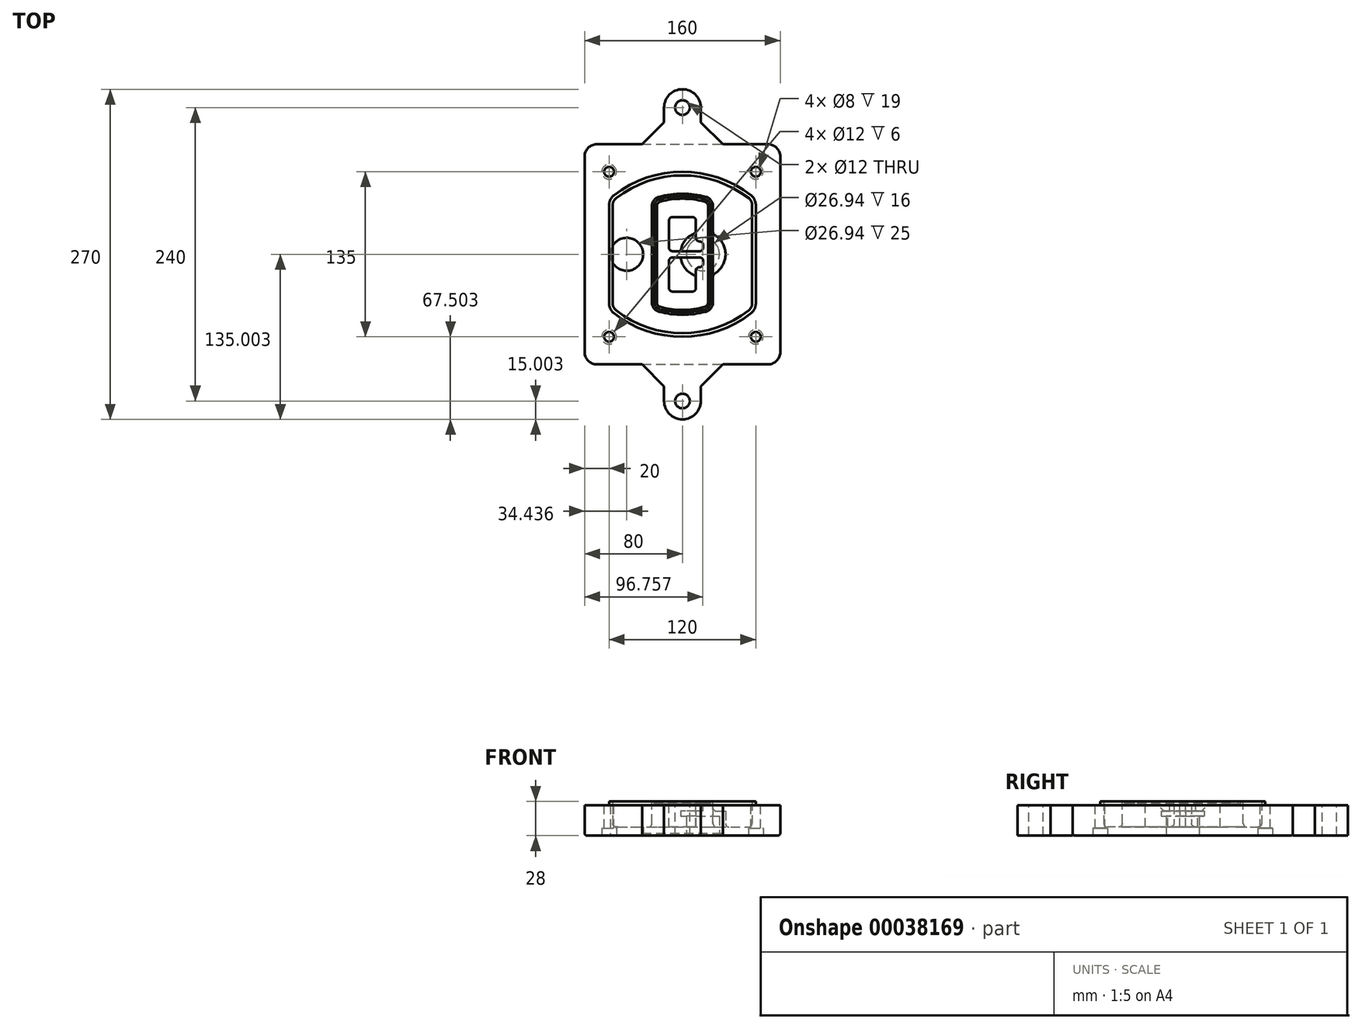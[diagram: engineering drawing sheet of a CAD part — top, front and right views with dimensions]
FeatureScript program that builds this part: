
annotation { "Feature Type Name" : "Feature", "Feature Type Description" : "" }
export const myFeature = defineFeature(function(context is Context, id is Id, definition is map)
    precondition{}
    {
        {
            var Q0;
            Q0=qCreatedBy(makeId("Top.planeOp"),FACE);
            var sketch = newSketch(context, id + "F0", { "sketchPlane" : qUnion([Q0])});
            skPoint(sketch, "E0.rect.middle", {"position": v(0, 0) * mm});
            skLineSegment(sketch, "E1.bottom", {"start": v(24.05, 28.38) * mm, "end": v(164.05, 28.38) * mm});
            skLineSegment(sketch, "E1.top", {"start": v(24.05, 208.38) * mm, "end": v(164.05, 208.38) * mm});
            skLineSegment(sketch, "E1.left", {"start": v(14.05, 38.38) * mm, "end": v(14.05, 198.38) * mm});
            skLineSegment(sketch, "E1.right", {"start": v(174.05, 38.38) * mm, "end": v(174.05, 198.38) * mm});
            skLineSegment(sketch, "E2", {"start": v(14.05, 208.38) * mm, "end": v(174.05, 28.38) * mm, "construction": true});
            skLineSegment(sketch, "E3", {"start": v(174.05, 208.38) * mm, "end": v(14.05, 28.38) * mm, "construction": true});
            skCircle(sketch, "E4", {"center": v(34.05, 185.88) * mm, "radius": 4 * mm});
            skCircle(sketch, "E5", {"center": v(154.05, 185.88) * mm, "radius": 4 * mm});
            skCircle(sketch, "E6", {"center": v(154.05, 50.88) * mm, "radius": 4 * mm});
            skCircle(sketch, "E7", {"center": v(34.05, 50.88) * mm, "radius": 4 * mm});
            skLineSegment(sketch, "E8", {"start": v(34.05, 185.88) * mm, "end": v(154.05, 185.88) * mm, "construction": true});
            skLineSegment(sketch, "E9", {"start": v(154.05, 185.88) * mm, "end": v(154.05, 50.88) * mm, "construction": true});
            skLineSegment(sketch, "E10", {"start": v(154.05, 50.88) * mm, "end": v(34.05, 50.88) * mm, "construction": true});
            skLineSegment(sketch, "E11", {"start": v(34.05, 50.88) * mm, "end": v(34.05, 185.88) * mm, "construction": true});
            skLineSegment(sketch, "E12", {"start": v(34.05, 158.68) * mm, "end": v(34.05, 78.09) * mm});
            skLineSegment(sketch, "E13", {"start": v(154.05, 158.68) * mm, "end": v(154.05, 78.09) * mm});
            skArc(sketch, "E14", {"start": v(150.2, 166.56) * mm, "mid": v(94.05, 185.88) * mm, "end": v(37.9, 166.56) * mm});
            skArc(sketch, "E15", {"start": v(37.9, 70.2) * mm, "mid": v(94.05, 50.88) * mm, "end": v(150.2, 70.2) * mm});
            skLineSegment(sketch, "E16", {"start": v(34.05, 118.38) * mm, "end": v(154.05, 118.38) * mm, "construction": true});
            skPoint(sketch, "E17.visualSharp", {"position": v(34.05, 73.38) * mm});
            skArc(sketch, "E17.filletArc", {"start": v(34.05, 78.09) * mm, "mid": v(35.06, 73.7) * mm, "end": v(37.9, 70.2) * mm});
            skPoint(sketch, "E18.visualSharp", {"position": v(34.05, 163.38) * mm});
            skArc(sketch, "E18.filletArc", {"start": v(37.9, 166.56) * mm, "mid": v(35.06, 163.06) * mm, "end": v(34.05, 158.68) * mm});
            skPoint(sketch, "E19.visualSharp", {"position": v(154.05, 163.38) * mm});
            skArc(sketch, "E19.filletArc", {"start": v(154.05, 158.68) * mm, "mid": v(153.04, 163.06) * mm, "end": v(150.2, 166.56) * mm});
            skPoint(sketch, "E20.visualSharp", {"position": v(154.05, 73.38) * mm});
            skArc(sketch, "E20.filletArc", {"start": v(150.2, 70.2) * mm, "mid": v(153.04, 73.7) * mm, "end": v(154.05, 78.09) * mm});
            skPoint(sketch, "E21.visualSharp", {"position": v(14.05, 208.38) * mm});
            skArc(sketch, "E21.filletArc", {"start": v(24.05, 208.38) * mm, "mid": v(16.98, 205.45) * mm, "end": v(14.05, 198.38) * mm});
            skPoint(sketch, "E22.visualSharp", {"position": v(174.05, 208.38) * mm});
            skArc(sketch, "E22.filletArc", {"start": v(174.05, 198.38) * mm, "mid": v(171.12, 205.45) * mm, "end": v(164.05, 208.38) * mm});
            skPoint(sketch, "E23.visualSharp", {"position": v(174.05, 28.38) * mm});
            skArc(sketch, "E23.filletArc", {"start": v(164.05, 28.38) * mm, "mid": v(171.12, 31.31) * mm, "end": v(174.05, 38.38) * mm});
            skPoint(sketch, "E24.visualSharp", {"position": v(14.05, 28.38) * mm});
            skArc(sketch, "E24.filletArc", {"start": v(14.05, 38.38) * mm, "mid": v(16.98, 31.31) * mm, "end": v(24.05, 28.38) * mm});
            skArc(sketch, "E25.0", {"start": v(151.05, 158.68) * mm, "mid": v(150.34, 161.75) * mm, "end": v(148.36, 164.2) * mm});
            skLineSegment(sketch, "E25.1", {"start": v(151.05, 158.68) * mm, "end": v(151.05, 78.09) * mm});
            skArc(sketch, "E25.2", {"start": v(148.36, 72.57) * mm, "mid": v(150.34, 75.02) * mm, "end": v(151.05, 78.09) * mm});
            skArc(sketch, "E25.3", {"start": v(39.74, 72.57) * mm, "mid": v(94.05, 53.88) * mm, "end": v(148.36, 72.57) * mm});
            skArc(sketch, "E25.4", {"start": v(37.05, 78.09) * mm, "mid": v(37.76, 75.02) * mm, "end": v(39.74, 72.57) * mm});
            skArc(sketch, "E25.5", {"start": v(148.36, 164.2) * mm, "mid": v(94.05, 182.88) * mm, "end": v(39.74, 164.2) * mm});
            skLineSegment(sketch, "E25.6", {"start": v(37.05, 158.68) * mm, "end": v(37.05, 78.09) * mm});
            skArc(sketch, "E25.7", {"start": v(39.74, 164.2) * mm, "mid": v(37.76, 161.75) * mm, "end": v(37.05, 158.68) * mm});
            skArc(sketch, "E26.0", {"start": v(35.43, 169.71) * mm, "mid": v(31.47, 164.82) * mm, "end": v(30.05, 158.68) * mm});
            skArc(sketch, "E26.1", {"start": v(152.67, 169.71) * mm, "mid": v(94.05, 189.88) * mm, "end": v(35.43, 169.71) * mm});
            skArc(sketch, "E26.2", {"start": v(158.05, 158.68) * mm, "mid": v(156.63, 164.82) * mm, "end": v(152.67, 169.71) * mm});
            skLineSegment(sketch, "E26.3", {"start": v(158.05, 158.68) * mm, "end": v(158.05, 78.09) * mm});
            skArc(sketch, "E26.4", {"start": v(152.67, 67.05) * mm, "mid": v(156.63, 71.95) * mm, "end": v(158.05, 78.09) * mm});
            skLineSegment(sketch, "E26.5", {"start": v(30.05, 158.68) * mm, "end": v(30.05, 78.09) * mm});
            skArc(sketch, "E26.6", {"start": v(35.43, 67.05) * mm, "mid": v(94.05, 46.88) * mm, "end": v(152.67, 67.05) * mm});
            skArc(sketch, "E26.7", {"start": v(30.05, 78.09) * mm, "mid": v(31.47, 71.95) * mm, "end": v(35.43, 67.05) * mm});
            skSolve(sketch);
        }
        {
            var Q0;
            Q0=makeQuery(id+"F0.imprint","IMPRINT",FACE,{"disambiguationData":[TD([[makeQuery(id+"F0.imprint","IMPRINT",EDGE,{"derivedFrom":sQuery(id+"F0.wireOp",EDGE,"E1.bottom")}),1.0]])]});
            var Q1;
            Q1=makeQuery(id+"F0.imprint","IMPRINT",FACE,{"disambiguationData":[TD([[makeQuery(id+"F0.imprint","IMPRINT",EDGE,{"derivedFrom":sQuery(id+"F0.wireOp",EDGE,"E12")}),1.0]])]});
            var Q2;
            Q2=makeQuery(id+"F0.imprint","IMPRINT",FACE,{"disambiguationData":[TD([[makeQuery(id+"F0.imprint","IMPRINT",EDGE,{"derivedFrom":sQuery(id+"F0.wireOp",EDGE,"E25.0")}),1.0]])]});
            var Q3;
            Q3=makeQuery(id+"F0.imprint","IMPRINT",FACE,{"disambiguationData":[TD([[makeQuery(id+"F0.imprint","IMPRINT",EDGE,{"derivedFrom":sQuery(id+"F0.wireOp",EDGE,"E12")}),-1.0]])]});
            extrude(context, id + "F1", {"entities" : qUnion([Q0, Q1, Q2, Q3]), "oppositeDirection" : true, "depth" : 25 * mm});
        }
        {
            var Q0;
            Q0=makeQuery(id+"F0.imprint","IMPRINT",FACE,{"disambiguationData":[TD([[makeQuery(id+"F0.imprint","IMPRINT",EDGE,{"derivedFrom":sQuery(id+"F0.wireOp",EDGE,"E12")}),1.0]])]});
            extrude(context, id + "F2", {"entities" : qUnion([Q0]), "operationType" : NewBodyOperationType.ADD, "depth" : 3 * mm});
        }
        {
            var Q0;
            Q0=makeQuery(id+"F0.imprint","IMPRINT",FACE,{"disambiguationData":[TD([[makeQuery(id+"F0.imprint","IMPRINT",EDGE,{"derivedFrom":sQuery(id+"F0.wireOp",EDGE,"E25.0")}),1.0]])]});
            extrude(context, id + "F3", {"entities" : qUnion([Q0]), "operationType" : NewBodyOperationType.REMOVE, "oppositeDirection" : true, "depth" : 18 * mm});
        }
        {
            var Q0;
            Q0=makeQuery(id+"F2.opExtrude","CAP_FACE",FACE,{"disambiguationData":[OSD([sQuery(id+"F0.wireOp",EDGE,"E12"),sQuery(id+"F0.wireOp",EDGE,"E13"),sQuery(id+"F0.wireOp",EDGE,"E14"),sQuery(id+"F0.wireOp",EDGE,"E15"),sQuery(id+"F0.wireOp",EDGE,"E17.filletArc"),sQuery(id+"F0.wireOp",EDGE,"E18.filletArc"),sQuery(id+"F0.wireOp",EDGE,"E19.filletArc"),sQuery(id+"F0.wireOp",EDGE,"E20.filletArc"),sQuery(id+"F0.wireOp",EDGE,"E25.0"),sQuery(id+"F0.wireOp",EDGE,"E25.1"),sQuery(id+"F0.wireOp",EDGE,"E25.2"),sQuery(id+"F0.wireOp",EDGE,"E25.3"),sQuery(id+"F0.wireOp",EDGE,"E25.4"),sQuery(id+"F0.wireOp",EDGE,"E25.5"),sQuery(id+"F0.wireOp",EDGE,"E25.6"),sQuery(id+"F0.wireOp",EDGE,"E25.7")])],"isStart":false});
            var sketch = newSketch(context, id + "F4", { "sketchPlane" : qUnion([Q0])});
            skArc(sketch, "E27.0", {"start": v(74.97, 71.41) * mm, "mid": v(94.05, 68.88) * mm, "end": v(113.13, 71.41) * mm});
            skArc(sketch, "E28.0", {"start": v(113.13, 165.35) * mm, "mid": v(94.05, 167.88) * mm, "end": v(74.97, 165.35) * mm});
            skLineSegment(sketch, "E29", {"start": v(69.05, 157.63) * mm, "end": v(69.05, 79.14) * mm});
            skLineSegment(sketch, "E30", {"start": v(119.05, 157.63) * mm, "end": v(119.05, 79.14) * mm});
            skLineSegment(sketch, "E31", {"start": v(69.05, 163.48) * mm, "end": v(119.05, 163.48) * mm, "construction": true});
            skLineSegment(sketch, "E32", {"start": v(69.05, 73.28) * mm, "end": v(119.05, 73.28) * mm, "construction": true});
            skPoint(sketch, "E33.visualSharp", {"position": v(69.05, 163.48) * mm});
            skArc(sketch, "E33.filletArc", {"start": v(74.97, 165.35) * mm, "mid": v(70.7, 162.5) * mm, "end": v(69.05, 157.63) * mm});
            skPoint(sketch, "E34.visualSharp", {"position": v(119.05, 163.48) * mm});
            skArc(sketch, "E34.filletArc", {"start": v(119.05, 157.63) * mm, "mid": v(117.4, 162.5) * mm, "end": v(113.13, 165.35) * mm});
            skPoint(sketch, "E35.visualSharp", {"position": v(119.05, 73.28) * mm});
            skArc(sketch, "E35.filletArc", {"start": v(113.13, 71.41) * mm, "mid": v(117.4, 74.27) * mm, "end": v(119.05, 79.14) * mm});
            skPoint(sketch, "E36.visualSharp", {"position": v(69.05, 73.28) * mm});
            skArc(sketch, "E36.filletArc", {"start": v(69.05, 79.14) * mm, "mid": v(70.7, 74.27) * mm, "end": v(74.97, 71.41) * mm});
            skArc(sketch, "E37.0", {"start": v(148.36, 164.2) * mm, "mid": v(94.05, 182.88) * mm, "end": v(39.74, 164.2) * mm});
            skArc(sketch, "E37.1", {"start": v(39.74, 164.2) * mm, "mid": v(37.76, 161.75) * mm, "end": v(37.05, 158.68) * mm});
            skLineSegment(sketch, "E37.2", {"start": v(37.05, 158.68) * mm, "end": v(37.05, 78.09) * mm});
            skArc(sketch, "E37.3", {"start": v(37.05, 78.09) * mm, "mid": v(37.76, 75.02) * mm, "end": v(39.74, 72.57) * mm});
            skArc(sketch, "E37.4", {"start": v(39.74, 72.57) * mm, "mid": v(94.05, 53.88) * mm, "end": v(148.36, 72.57) * mm});
            skArc(sketch, "E37.5", {"start": v(148.36, 72.57) * mm, "mid": v(150.34, 75.02) * mm, "end": v(151.05, 78.09) * mm});
            skLineSegment(sketch, "E37.6", {"start": v(151.05, 158.68) * mm, "end": v(151.05, 78.09) * mm});
            skArc(sketch, "E37.7", {"start": v(151.05, 158.68) * mm, "mid": v(150.34, 161.75) * mm, "end": v(148.36, 164.2) * mm});
            skLineSegment(sketch, "E38.0", {"start": v(117.05, 157.63) * mm, "end": v(117.05, 79.14) * mm});
            skArc(sketch, "E38.1", {"start": v(112.61, 73.34) * mm, "mid": v(115.81, 75.49) * mm, "end": v(117.05, 79.14) * mm});
            skArc(sketch, "E38.2", {"start": v(75.49, 73.34) * mm, "mid": v(94.05, 70.88) * mm, "end": v(112.61, 73.34) * mm});
            skArc(sketch, "E38.3", {"start": v(71.05, 79.14) * mm, "mid": v(72.29, 75.49) * mm, "end": v(75.49, 73.34) * mm});
            skLineSegment(sketch, "E38.4", {"start": v(71.05, 157.63) * mm, "end": v(71.05, 79.14) * mm});
            skArc(sketch, "E38.5", {"start": v(117.05, 157.63) * mm, "mid": v(115.81, 161.28) * mm, "end": v(112.61, 163.42) * mm});
            skArc(sketch, "E38.6", {"start": v(75.49, 163.42) * mm, "mid": v(72.29, 161.28) * mm, "end": v(71.05, 157.63) * mm});
            skArc(sketch, "E38.7", {"start": v(112.61, 163.42) * mm, "mid": v(94.05, 165.88) * mm, "end": v(75.49, 163.42) * mm});
            skArc(sketch, "E39.0", {"start": v(115.05, 157.63) * mm, "mid": v(114.23, 160.06) * mm, "end": v(112.1, 161.5) * mm});
            skLineSegment(sketch, "E39.1", {"start": v(115.05, 157.63) * mm, "end": v(115.05, 79.14) * mm});
            skArc(sketch, "E39.2", {"start": v(112.1, 75.27) * mm, "mid": v(114.23, 76.7) * mm, "end": v(115.05, 79.14) * mm});
            skArc(sketch, "E39.3", {"start": v(76, 75.27) * mm, "mid": v(94.05, 72.88) * mm, "end": v(112.1, 75.27) * mm});
            skArc(sketch, "E39.4", {"start": v(73.05, 79.14) * mm, "mid": v(73.87, 76.7) * mm, "end": v(76, 75.27) * mm});
            skArc(sketch, "E39.5", {"start": v(112.1, 161.5) * mm, "mid": v(94.05, 163.88) * mm, "end": v(76, 161.5) * mm});
            skLineSegment(sketch, "E39.6", {"start": v(73.05, 157.63) * mm, "end": v(73.05, 79.14) * mm});
            skArc(sketch, "E39.7", {"start": v(76, 161.5) * mm, "mid": v(73.87, 160.06) * mm, "end": v(73.05, 157.63) * mm});
            skLineSegment(sketch, "E40", {"start": v(69.05, 118.38) * mm, "end": v(119.05, 118.38) * mm, "construction": true});
            skLineSegment(sketch, "E41", {"start": v(83.05, 123.88) * mm, "end": v(83.05, 145.88) * mm});
            skLineSegment(sketch, "E42", {"start": v(86.05, 148.88) * mm, "end": v(102.05, 148.88) * mm});
            skLineSegment(sketch, "E43", {"start": v(105.05, 145.88) * mm, "end": v(105.05, 131.88) * mm});
            skLineSegment(sketch, "E44", {"start": v(108.05, 128.88) * mm, "end": v(108.05, 128.88) * mm});
            skLineSegment(sketch, "E45", {"start": v(111.05, 125.88) * mm, "end": v(111.05, 123.88) * mm});
            skLineSegment(sketch, "E46", {"start": v(108.05, 120.88) * mm, "end": v(86.05, 120.88) * mm});
            skPoint(sketch, "E47.visualSharp", {"position": v(83.05, 148.88) * mm});
            skArc(sketch, "E47.filletArc", {"start": v(86.05, 148.88) * mm, "mid": v(83.93, 148) * mm, "end": v(83.05, 145.88) * mm});
            skPoint(sketch, "E48.visualSharp", {"position": v(105.05, 148.88) * mm});
            skArc(sketch, "E48.filletArc", {"start": v(105.05, 145.88) * mm, "mid": v(104.17, 148) * mm, "end": v(102.05, 148.88) * mm});
            skPoint(sketch, "E49.visualSharp", {"position": v(105.05, 128.88) * mm});
            skArc(sketch, "E49.filletArc", {"start": v(105.05, 131.88) * mm, "mid": v(105.93, 129.76) * mm, "end": v(108.05, 128.88) * mm});
            skPoint(sketch, "E50.visualSharp", {"position": v(111.05, 128.88) * mm});
            skArc(sketch, "E50.filletArc", {"start": v(111.05, 125.88) * mm, "mid": v(110.17, 128) * mm, "end": v(108.05, 128.88) * mm});
            skPoint(sketch, "E51.visualSharp", {"position": v(111.05, 120.88) * mm});
            skArc(sketch, "E51.filletArc", {"start": v(108.05, 120.88) * mm, "mid": v(110.17, 121.76) * mm, "end": v(111.05, 123.88) * mm});
            skPoint(sketch, "E52.visualSharp", {"position": v(83.05, 120.88) * mm});
            skArc(sketch, "E52.filletArc", {"start": v(83.05, 123.88) * mm, "mid": v(83.93, 121.76) * mm, "end": v(86.05, 120.88) * mm});
            skLineSegment(sketch, "E53.0.MirrorCS", {"start": v(108.05, 115.88) * mm, "end": v(86.05, 115.88) * mm});
            skArc(sketch, "E54.0.MirrorCS", {"start": v(83.05, 112.88) * mm, "mid": v(83.93, 115) * mm, "end": v(86.05, 115.88) * mm});
            skLineSegment(sketch, "E55.0.MirrorCS", {"start": v(83.05, 112.88) * mm, "end": v(83.05, 90.88) * mm});
            skArc(sketch, "E56.0.MirrorCS", {"start": v(86.05, 87.88) * mm, "mid": v(83.93, 88.76) * mm, "end": v(83.05, 90.88) * mm});
            skLineSegment(sketch, "E57.0.MirrorCS", {"start": v(86.05, 87.88) * mm, "end": v(102.05, 87.88) * mm});
            skArc(sketch, "E58.0.MirrorCS", {"start": v(105.05, 90.88) * mm, "mid": v(104.17, 88.76) * mm, "end": v(102.05, 87.88) * mm});
            skLineSegment(sketch, "E59.0.MirrorCS", {"start": v(105.05, 90.88) * mm, "end": v(105.05, 104.88) * mm});
            skArc(sketch, "E60.0.MirrorCS", {"start": v(105.05, 104.88) * mm, "mid": v(105.93, 107) * mm, "end": v(108.05, 107.88) * mm});
            skArc(sketch, "E61.0.MirrorCS", {"start": v(111.05, 110.88) * mm, "mid": v(110.17, 108.76) * mm, "end": v(108.05, 107.88) * mm});
            skLineSegment(sketch, "E62.0.MirrorCS", {"start": v(111.05, 110.88) * mm, "end": v(111.05, 112.88) * mm});
            skArc(sketch, "E63.0.MirrorCS", {"start": v(108.05, 115.88) * mm, "mid": v(110.17, 115) * mm, "end": v(111.05, 112.88) * mm});
            skSolve(sketch);
        }
        {
            var Q0;
            Q0=makeQuery(id+"F4.imprint","IMPRINT",FACE,{"disambiguationData":[TD([[makeQuery(id+"F4.imprint","IMPRINT",EDGE,{"derivedFrom":sQuery(id+"F4.wireOp",EDGE,"E27.0")}),1.0]])]});
            var Q1;
            Q1=makeQuery(id+"F4.imprint","IMPRINT",FACE,{"disambiguationData":[TD([[makeQuery(id+"F4.imprint","IMPRINT",EDGE,{"derivedFrom":sQuery(id+"F4.wireOp",EDGE,"E38.0")}),-1.0]])]});
            var Q2;
            Q2=makeQuery(id+"F4.imprint","IMPRINT",FACE,{"disambiguationData":[TD([[makeQuery(id+"F4.imprint","IMPRINT",EDGE,{"derivedFrom":sQuery(id+"F4.wireOp",EDGE,"E39.0")}),1.0]])]});
            extrude(context, id + "F5", {"entities" : qUnion([Q0, Q1, Q2]), "operationType" : NewBodyOperationType.ADD, "endBound" : BoundingType.UP_TO_NEXT, "oppositeDirection" : true, "depth" : 25 * mm});
        }
        {
            var Q0;
            Q0=makeQuery(id+"F4.imprint","IMPRINT",FACE,{"disambiguationData":[TD([[makeQuery(id+"F4.imprint","IMPRINT",EDGE,{"derivedFrom":sQuery(id+"F4.wireOp",EDGE,"E38.0")}),-1.0]])]});
            extrude(context, id + "F6", {"entities" : qUnion([Q0]), "operationType" : NewBodyOperationType.REMOVE, "oppositeDirection" : true, "depth" : 2 * mm});
        }
        {
            var Q0;
            Q0=makeQuery(id+"F1.opExtrude","CAP_FACE",FACE,{"disambiguationData":[OSD([sQuery(id+"F0.wireOp",EDGE,"E1.bottom"),sQuery(id+"F0.wireOp",EDGE,"E1.top"),sQuery(id+"F0.wireOp",EDGE,"E1.left"),sQuery(id+"F0.wireOp",EDGE,"E1.right"),sQuery(id+"F0.wireOp",EDGE,"E4"),sQuery(id+"F0.wireOp",EDGE,"E5"),sQuery(id+"F0.wireOp",EDGE,"E6"),sQuery(id+"F0.wireOp",EDGE,"E7"),sQuery(id+"F0.wireOp",EDGE,"E21.filletArc"),sQuery(id+"F0.wireOp",EDGE,"E22.filletArc"),sQuery(id+"F0.wireOp",EDGE,"E23.filletArc"),sQuery(id+"F0.wireOp",EDGE,"E24.filletArc")])],"isStart":false});
            var sketch = newSketch(context, id + "F7", { "sketchPlane" : qUnion([Q0])});
            skCircle(sketch, "E64", {"center": v(110.8, -118.38) * mm, "radius": 13.47 * mm});
            skCircle(sketch, "E65", {"center": v(48.49, -118.38) * mm, "radius": 13.47 * mm});
            skLineSegment(sketch, "E66", {"start": v(174.05, -118.38) * mm, "end": v(14.05, -118.38) * mm});
            skCircle(sketch, "E67", {"center": v(110.8, -118.38) * mm, "radius": 18.47 * mm});
            skCircle(sketch, "E68", {"center": v(154.05, -185.88) * mm, "radius": 6 * mm});
            skCircle(sketch, "E69", {"center": v(34.05, -185.88) * mm, "radius": 6 * mm});
            skCircle(sketch, "E70", {"center": v(34.05, -50.88) * mm, "radius": 6 * mm});
            skCircle(sketch, "E71", {"center": v(154.05, -50.88) * mm, "radius": 6 * mm});
            skSolve(sketch);
        }
        {
            var Q0;
            {var subQ1=sQuery(id+"F7.wireOp",EDGE,"E66");var subQ4=sQuery(id+"F7.wireOp",EDGE,"E64");var subQ6=makeQuery(id+"F7.imprint","INTERSECT",VERTEX,{"disambiguationData":[OD(0.0)],"derivedFrom":[subQ4,subQ1]});Q0=makeQuery(id+"F7.imprint","IMPRINT",FACE,{"disambiguationData":[TD([[makeQuery(id+"F7.imprint","IMPRINT",EDGE,{"disambiguationData":[TD([[subQ6,-1.0]])],"derivedFrom":subQ4}),-1.0]])]});}
            var Q1;
            {var subQ0=sQuery(id+"F7.wireOp",EDGE,"E66");var subQ1=sQuery(id+"F7.wireOp",EDGE,"E64");var subQ3=makeQuery(id+"F7.imprint","INTERSECT",VERTEX,{"disambiguationData":[OD(0.0)],"derivedFrom":[subQ1,subQ0]});Q1=makeQuery(id+"F7.imprint","IMPRINT",FACE,{"disambiguationData":[TD([[makeQuery(id+"F7.imprint","IMPRINT",EDGE,{"disambiguationData":[TD([[subQ3,-1.0]])],"derivedFrom":subQ1}),1.0]])]});}
            var Q2;
            {var subQ0=sQuery(id+"F7.wireOp",EDGE,"E66");var subQ1=sQuery(id+"F7.wireOp",EDGE,"E64");var subQ3=makeQuery(id+"F7.imprint","INTERSECT",VERTEX,{"disambiguationData":[OD(0.0)],"derivedFrom":[subQ1,subQ0]});Q2=makeQuery(id+"F7.imprint","IMPRINT",FACE,{"disambiguationData":[TD([[makeQuery(id+"F7.imprint","IMPRINT",EDGE,{"disambiguationData":[TD([[subQ3,1.0]])],"derivedFrom":subQ1}),1.0]])]});}
            var Q3;
            {var subQ1=sQuery(id+"F7.wireOp",EDGE,"E66");var subQ4=sQuery(id+"F7.wireOp",EDGE,"E64");var subQ6=makeQuery(id+"F7.imprint","INTERSECT",VERTEX,{"disambiguationData":[OD(0.0)],"derivedFrom":[subQ4,subQ1]});Q3=makeQuery(id+"F7.imprint","IMPRINT",FACE,{"disambiguationData":[TD([[makeQuery(id+"F7.imprint","IMPRINT",EDGE,{"disambiguationData":[TD([[subQ6,1.0]])],"derivedFrom":subQ4}),-1.0]])]});}
            extrude(context, id + "F8", {"entities" : qUnion([Q0, Q1, Q2, Q3]), "operationType" : NewBodyOperationType.ADD, "oppositeDirection" : true, "depth" : 20 * mm});
        }
        {
            var Q0;
            {var subQ0=sQuery(id+"F7.wireOp",EDGE,"E66");var subQ1=sQuery(id+"F7.wireOp",EDGE,"E64");var subQ3=makeQuery(id+"F7.imprint","INTERSECT",VERTEX,{"disambiguationData":[OD(0.0)],"derivedFrom":[subQ1,subQ0]});Q0=makeQuery(id+"F7.imprint","IMPRINT",FACE,{"disambiguationData":[TD([[makeQuery(id+"F7.imprint","IMPRINT",EDGE,{"disambiguationData":[TD([[subQ3,-1.0]])],"derivedFrom":subQ1}),1.0]])]});}
            var Q1;
            {var subQ0=sQuery(id+"F7.wireOp",EDGE,"E66");var subQ1=sQuery(id+"F7.wireOp",EDGE,"E64");var subQ3=makeQuery(id+"F7.imprint","INTERSECT",VERTEX,{"disambiguationData":[OD(0.0)],"derivedFrom":[subQ1,subQ0]});Q1=makeQuery(id+"F7.imprint","IMPRINT",FACE,{"disambiguationData":[TD([[makeQuery(id+"F7.imprint","IMPRINT",EDGE,{"disambiguationData":[TD([[subQ3,1.0]])],"derivedFrom":subQ1}),1.0]])]});}
            extrude(context, id + "F9", {"entities" : qUnion([Q0, Q1]), "operationType" : NewBodyOperationType.REMOVE, "oppositeDirection" : true, "depth" : 16 * mm});
        }
        {
            var Q0;
            {var subQ0=sQuery(id+"F7.wireOp",EDGE,"E66");var subQ1=sQuery(id+"F7.wireOp",EDGE,"E65");var subQ3=makeQuery(id+"F7.imprint","INTERSECT",VERTEX,{"disambiguationData":[OD(0.0)],"derivedFrom":[subQ1,subQ0]});Q0=makeQuery(id+"F7.imprint","IMPRINT",FACE,{"disambiguationData":[TD([[makeQuery(id+"F7.imprint","IMPRINT",EDGE,{"disambiguationData":[TD([[subQ3,-1.0]])],"derivedFrom":subQ1}),1.0]])]});}
            var Q1;
            {var subQ0=sQuery(id+"F7.wireOp",EDGE,"E66");var subQ1=sQuery(id+"F7.wireOp",EDGE,"E65");var subQ3=makeQuery(id+"F7.imprint","INTERSECT",VERTEX,{"disambiguationData":[OD(0.0)],"derivedFrom":[subQ1,subQ0]});Q1=makeQuery(id+"F7.imprint","IMPRINT",FACE,{"disambiguationData":[TD([[makeQuery(id+"F7.imprint","IMPRINT",EDGE,{"disambiguationData":[TD([[subQ3,1.0]])],"derivedFrom":subQ1}),1.0]])]});}
            extrude(context, id + "F10", {"entities" : qUnion([Q0, Q1]), "operationType" : NewBodyOperationType.REMOVE, "oppositeDirection" : true, "depth" : 25 * mm});
        }
        {
            var Q0;
            Q0=makeQuery(id+"F7.imprint","IMPRINT",FACE,{"disambiguationData":[TD([[makeQuery(id+"F7.imprint","IMPRINT",EDGE,{"derivedFrom":sQuery(id+"F7.wireOp",EDGE,"E68")}),1.0]])]});
            var Q1;
            Q1=makeQuery(id+"F7.imprint","IMPRINT",FACE,{"disambiguationData":[TD([[makeQuery(id+"F7.imprint","IMPRINT",EDGE,{"derivedFrom":makeQuery(id+"F1.opExtrude","CAP_EDGE",EDGE,{"disambiguationData":[OSD([sQuery(id+"F0.wireOp",EDGE,"E5")])],"isStart":false})}),-1.0]])]});
            var Q2;
            Q2=makeQuery(id+"F7.imprint","IMPRINT",FACE,{"disambiguationData":[TD([[makeQuery(id+"F7.imprint","IMPRINT",EDGE,{"derivedFrom":sQuery(id+"F7.wireOp",EDGE,"E69")}),1.0]])]});
            var Q3;
            Q3=makeQuery(id+"F7.imprint","IMPRINT",FACE,{"disambiguationData":[TD([[makeQuery(id+"F7.imprint","IMPRINT",EDGE,{"derivedFrom":makeQuery(id+"F1.opExtrude","CAP_EDGE",EDGE,{"disambiguationData":[OSD([sQuery(id+"F0.wireOp",EDGE,"E4")])],"isStart":false})}),-1.0]])]});
            var Q4;
            Q4=makeQuery(id+"F7.imprint","IMPRINT",FACE,{"disambiguationData":[TD([[makeQuery(id+"F7.imprint","IMPRINT",EDGE,{"derivedFrom":sQuery(id+"F7.wireOp",EDGE,"E70")}),1.0]])]});
            var Q5;
            Q5=makeQuery(id+"F7.imprint","IMPRINT",FACE,{"disambiguationData":[TD([[makeQuery(id+"F7.imprint","IMPRINT",EDGE,{"derivedFrom":makeQuery(id+"F1.opExtrude","CAP_EDGE",EDGE,{"disambiguationData":[OSD([sQuery(id+"F0.wireOp",EDGE,"E7")])],"isStart":false})}),-1.0]])]});
            var Q6;
            Q6=makeQuery(id+"F7.imprint","IMPRINT",FACE,{"disambiguationData":[TD([[makeQuery(id+"F7.imprint","IMPRINT",EDGE,{"derivedFrom":sQuery(id+"F7.wireOp",EDGE,"E71")}),1.0]])]});
            var Q7;
            Q7=makeQuery(id+"F7.imprint","IMPRINT",FACE,{"disambiguationData":[TD([[makeQuery(id+"F7.imprint","IMPRINT",EDGE,{"derivedFrom":makeQuery(id+"F1.opExtrude","CAP_EDGE",EDGE,{"disambiguationData":[OSD([sQuery(id+"F0.wireOp",EDGE,"E6")])],"isStart":false})}),-1.0]])]});
            extrude(context, id + "F11", {"entities" : qUnion([Q0, Q1, Q2, Q3, Q4, Q5, Q6, Q7]), "operationType" : NewBodyOperationType.REMOVE, "oppositeDirection" : true, "depth" : 6 * mm});
        }
        {
            var Q0;
            Q0=makeQuery(id+"F9.boolean.opBoolean","COPY",FACE,{"derivedFrom":makeQuery(id+"F9.opExtrude","CAP_FACE",FACE,{"disambiguationData":[OSD([sQuery(id+"F7.wireOp",EDGE,"E64")])],"isStart":false})});
            var sketch = newSketch(context, id + "F12", { "sketchPlane" : qUnion([Q0])});
            skArc(sketch, "E72.0", {"start": v(105.05, -100.83) * mm, "mid": v(96.62, -106.56) * mm, "end": v(92.5, -115.88) * mm});
            skArc(sketch, "E72.1", {"start": v(92.5, -120.88) * mm, "mid": v(96.62, -130.2) * mm, "end": v(105.05, -135.93) * mm});
            skLineSegment(sketch, "E73", {"start": v(92.5, -120.88) * mm, "end": v(108.05, -120.88) * mm});
            skLineSegment(sketch, "E74.0", {"start": v(108.05, -115.88) * mm, "end": v(92.5, -115.88) * mm});
            skArc(sketch, "E74.1", {"start": v(108.05, -115.88) * mm, "mid": v(110.17, -115) * mm, "end": v(111.05, -112.88) * mm});
            skLineSegment(sketch, "E74.2", {"start": v(111.05, -110.88) * mm, "end": v(111.05, -112.88) * mm});
            skArc(sketch, "E74.3", {"start": v(111.05, -110.88) * mm, "mid": v(110.17, -108.76) * mm, "end": v(108.05, -107.88) * mm});
            skArc(sketch, "E74.4", {"start": v(105.05, -104.88) * mm, "mid": v(105.93, -107) * mm, "end": v(108.05, -107.88) * mm});
            skLineSegment(sketch, "E74.5", {"start": v(105.05, -100.83) * mm, "end": v(105.05, -104.88) * mm});
            skLineSegment(sketch, "E74.7", {"start": v(108.05, -120.88) * mm, "end": v(92.5, -120.88) * mm});
            skArc(sketch, "E74.8", {"start": v(108.05, -120.88) * mm, "mid": v(110.17, -121.76) * mm, "end": v(111.05, -123.88) * mm});
            skLineSegment(sketch, "E74.9", {"start": v(111.05, -125.88) * mm, "end": v(111.05, -123.88) * mm});
            skArc(sketch, "E74.10", {"start": v(111.05, -125.88) * mm, "mid": v(110.17, -128) * mm, "end": v(108.05, -128.88) * mm});
            skArc(sketch, "E74.11", {"start": v(105.05, -131.88) * mm, "mid": v(105.93, -129.76) * mm, "end": v(108.05, -128.88) * mm});
            skLineSegment(sketch, "E74.12", {"start": v(105.05, -135.93) * mm, "end": v(105.05, -131.88) * mm});
            skPoint(sketch, "E75.orphan", {"position": v(105.05, -145.88) * mm});
            skPoint(sketch, "E76.orphan", {"position": v(86.05, -120.88) * mm});
            skPoint(sketch, "E77.orphan", {"position": v(86.05, -115.88) * mm});
            skPoint(sketch, "E78.orphan", {"position": v(105.05, -90.88) * mm});
            skSolve(sketch);
        }
        {
            var Q0;
            {var subQ7=sQuery(id+"F12.wireOp",EDGE,"E72.0");var subQ14=sQuery(id+"F12.wireOp",EDGE,"E72.1");var subQ16=sQuery(id+"F12.wireOp",EDGE,"E74.1");var subQ18=sQuery(id+"F12.wireOp",EDGE,"E74.8");Q0=qUnion([makeQuery(id+"F12.imprint","IMPRINT",FACE,{"disambiguationData":[TD([[makeQuery(id+"F12.imprint","IMPRINT",EDGE,{"derivedFrom":subQ7}),1.0]])]}),makeQuery(id+"F12.imprint","IMPRINT",FACE,{"disambiguationData":[TD([[makeQuery(id+"F12.imprint","IMPRINT",EDGE,{"derivedFrom":subQ14}),1.0]])]}),makeQuery(id+"F12.imprint","IMPRINT",FACE,{"disambiguationData":[TD([[makeQuery(id+"F12.imprint","IMPRINT",EDGE,{"derivedFrom":subQ16}),1.0]])]}),makeQuery(id+"F12.imprint","IMPRINT",FACE,{"disambiguationData":[TD([[makeQuery(id+"F12.imprint","IMPRINT",EDGE,{"derivedFrom":subQ18}),-1.0]])]})]);}
            var Q1;
            Q1=makeQuery(id+"F5.boolean.opBoolean","SPLIT",FACE,{"disambiguationData":[TD([makeQuery(id+"F5.opExtrude","SWEPT_FACE",FACE,{"disambiguationData":[OSD([sQuery(id+"F4.wireOp",EDGE,"E41")])]})])],"derivedFrom":makeQuery(id+"F3.boolean.opBoolean","COPY",FACE,{"derivedFrom":makeQuery(id+"F3.opExtrude","CAP_FACE",FACE,{"disambiguationData":[OSD([sQuery(id+"F0.wireOp",EDGE,"E25.0"),sQuery(id+"F0.wireOp",EDGE,"E25.1"),sQuery(id+"F0.wireOp",EDGE,"E25.2"),sQuery(id+"F0.wireOp",EDGE,"E25.3"),sQuery(id+"F0.wireOp",EDGE,"E25.4"),sQuery(id+"F0.wireOp",EDGE,"E25.5"),sQuery(id+"F0.wireOp",EDGE,"E25.6"),sQuery(id+"F0.wireOp",EDGE,"E25.7")])],"isStart":false})})});
            extrude(context, id + "F13", {"entities" : qUnion([Q0]), "operationType" : NewBodyOperationType.REMOVE, "endBound" : BoundingType.UP_TO_SURFACE, "endBoundEntityFace" : qUnion([Q1]), "depth" : 25 * mm});
        }
        {
            var Q0;
            Q0=makeQuery(id+"F3.boolean.opBoolean","COPY",EDGE,{"derivedFrom":makeQuery(id+"F3.opExtrude","CAP_EDGE",EDGE,{"disambiguationData":[OSD([sQuery(id+"F0.wireOp",EDGE,"E25.6")])],"isStart":false})});
            var Q1;
            Q1=makeQuery(id+"F8.boolean.opBoolean","INTERSECT",EDGE,{"derivedFrom":[makeQuery(id+"F5.opExtrude","SWEPT_FACE",FACE,{"disambiguationData":[OSD([sQuery(id+"F4.wireOp",EDGE,"E30")])]}),makeQuery(id+"F8.opExtrude","CAP_FACE",FACE,{"disambiguationData":[OSD([sQuery(id+"F7.wireOp",EDGE,"E67")])],"isStart":false})]});
            var Q2;
            Q2=makeQuery(id+"F8.boolean.opBoolean","INTERSECT",EDGE,{"disambiguationData":[OD(1.0)],"derivedFrom":[makeQuery(id+"F5.opExtrude","SWEPT_FACE",FACE,{"disambiguationData":[OSD([sQuery(id+"F4.wireOp",EDGE,"E30")])]}),makeQuery(id+"F8.opExtrude","SWEPT_FACE",FACE,{"disambiguationData":[OSD([sQuery(id+"F7.wireOp",EDGE,"E67")])]})]});
            var Q3;
            {var subQ0=sQuery(id+"F4.wireOp",EDGE,"E30");Q3=makeQuery(id+"F8.boolean.opBoolean","SPLIT",EDGE,{"disambiguationData":[TD([makeQuery(id+"F5.opExtrude","SWEPT_FACE",FACE,{"disambiguationData":[OSD([sQuery(id+"F4.wireOp",EDGE,"E35.filletArc")])]})])],"derivedFrom":makeQuery(id+"F5.opExtrude","CAP_EDGE",EDGE,{"disambiguationData":[OSD([subQ0])],"isStart":false})});}
            var Q4;
            {var subQ0=sQuery(id+"F0.wireOp",EDGE,"E25.7");var subQ1=sQuery(id+"F0.wireOp",EDGE,"E25.1");var subQ2=sQuery(id+"F0.wireOp",EDGE,"E25.6");var subQ3=sQuery(id+"F0.wireOp",EDGE,"E25.5");var subQ4=sQuery(id+"F0.wireOp",EDGE,"E25.4");var subQ5=sQuery(id+"F0.wireOp",EDGE,"E25.0");var subQ6=sQuery(id+"F0.wireOp",EDGE,"E25.2");var subQ7=sQuery(id+"F0.wireOp",EDGE,"E25.3");Q4=makeQuery(id+"F8.boolean.opBoolean","INTERSECT",EDGE,{"derivedFrom":[makeQuery(id+"F5.boolean.opBoolean","SPLIT",FACE,{"disambiguationData":[TD([makeQuery(id+"F2.opExtrude","SWEPT_FACE",FACE,{"disambiguationData":[OSD([subQ5])]})])],"derivedFrom":makeQuery(id+"F3.boolean.opBoolean","COPY",FACE,{"derivedFrom":makeQuery(id+"F3.opExtrude","CAP_FACE",FACE,{"disambiguationData":[OSD([subQ5,subQ1,subQ6,subQ7,subQ4,subQ3,subQ2,subQ0])],"isStart":false})})}),makeQuery(id+"F8.opExtrude","SWEPT_FACE",FACE,{"disambiguationData":[OSD([sQuery(id+"F7.wireOp",EDGE,"E67")])]})]});}
            var Q5;
            Q5=makeQuery(id+"F8.boolean.opBoolean","INTERSECT",EDGE,{"disambiguationData":[OD(0.0)],"derivedFrom":[makeQuery(id+"F5.opExtrude","SWEPT_FACE",FACE,{"disambiguationData":[OSD([sQuery(id+"F4.wireOp",EDGE,"E30")])]}),makeQuery(id+"F8.opExtrude","SWEPT_FACE",FACE,{"disambiguationData":[OSD([sQuery(id+"F7.wireOp",EDGE,"E67")])]})]});
            fillet(context, id + "F14", {"entities" : qUnion([Q0, Q1, Q2, Q3, Q4, Q5]), "radius" : 3 * mm, "tangentPropagation" : true, "allowEdgeOverflow" : false});
        }
        {
            var Q0;
            Q0=makeQuery(id+"F1.opExtrude","CAP_EDGE",EDGE,{"disambiguationData":[OSD([sQuery(id+"F0.wireOp",EDGE,"E1.bottom")])],"isStart":false});
            fillet(context, id + "F15", {"entities" : qUnion([Q0]), "radius" : 2 * mm, "tangentPropagation" : true, "allowEdgeOverflow" : false});
        }
        {
            var Q0;
            {var subQ0=sQuery(id+"F0.wireOp",EDGE,"E1.bottom");var subQ1=sQuery(id+"F0.wireOp",EDGE,"E1.top");var subQ2=sQuery(id+"F0.wireOp",EDGE,"E1.left");var subQ3=sQuery(id+"F0.wireOp",EDGE,"E1.right");var subQ4=sQuery(id+"F0.wireOp",EDGE,"E4");var subQ5=sQuery(id+"F0.wireOp",EDGE,"E5");var subQ6=sQuery(id+"F0.wireOp",EDGE,"E6");var subQ7=sQuery(id+"F0.wireOp",EDGE,"E7");var subQ8=sQuery(id+"F0.wireOp",EDGE,"E21.filletArc");var subQ9=sQuery(id+"F0.wireOp",EDGE,"E22.filletArc");var subQ10=sQuery(id+"F0.wireOp",EDGE,"E23.filletArc");var subQ11=sQuery(id+"F0.wireOp",EDGE,"E24.filletArc");Q0=makeQuery(id+"F2.boolean.opBoolean","SPLIT",FACE,{"disambiguationData":[TD([makeQuery(id+"F1.opExtrude","SWEPT_FACE",FACE,{"disambiguationData":[OSD([subQ0])]})])],"derivedFrom":makeQuery(id+"F1.opExtrude","CAP_FACE",FACE,{"disambiguationData":[OSD([subQ0,subQ1,subQ2,subQ3,subQ4,subQ5,subQ6,subQ7,subQ8,subQ9,subQ10,subQ11])],"isStart":true})});}
            var sketch = newSketch(context, id + "F16", { "sketchPlane" : qUnion([Q0])});
            skCircle(sketch, "E79.1", {"center": v(34.05, 185.88) * mm, "radius": 4 * mm});
            skCircle(sketch, "E79.2", {"center": v(154.05, 185.88) * mm, "radius": 4 * mm});
            skCircle(sketch, "E79.3", {"center": v(154.05, 50.88) * mm, "radius": 4 * mm});
            skCircle(sketch, "E79.4", {"center": v(34.05, 50.88) * mm, "radius": 4 * mm});
            skLineSegment(sketch, "E80.5", {"start": v(24.05, 208.38) * mm, "end": v(164.05, 208.38) * mm});
            skArc(sketch, "E80.6", {"start": v(174.05, 198.38) * mm, "mid": v(171.12, 205.45) * mm, "end": v(164.05, 208.38) * mm});
            skLineSegment(sketch, "E80.7", {"start": v(174.05, 38.38) * mm, "end": v(174.05, 198.38) * mm});
            skArc(sketch, "E80.8", {"start": v(164.05, 28.38) * mm, "mid": v(171.12, 31.31) * mm, "end": v(174.05, 38.38) * mm});
            skLineSegment(sketch, "E80.9", {"start": v(24.05, 28.38) * mm, "end": v(164.05, 28.38) * mm});
            skArc(sketch, "E80.10", {"start": v(14.05, 38.38) * mm, "mid": v(16.98, 31.31) * mm, "end": v(24.05, 28.38) * mm});
            skLineSegment(sketch, "E80.11", {"start": v(14.05, 38.38) * mm, "end": v(14.05, 198.38) * mm});
            skArc(sketch, "E80.12", {"start": v(24.05, 208.38) * mm, "mid": v(16.98, 205.45) * mm, "end": v(14.05, 198.38) * mm});
            skArc(sketch, "E80.13", {"start": v(150.2, 166.56) * mm, "mid": v(94.05, 185.88) * mm, "end": v(37.9, 166.56) * mm});
            skLineSegment(sketch, "E80.14", {"start": v(34.05, 158.68) * mm, "end": v(34.05, 78.09) * mm});
            skArc(sketch, "E80.15", {"start": v(37.9, 166.56) * mm, "mid": v(35.06, 163.06) * mm, "end": v(34.05, 158.68) * mm});
            skArc(sketch, "E80.16", {"start": v(34.05, 78.09) * mm, "mid": v(35.06, 73.7) * mm, "end": v(37.9, 70.2) * mm});
            skArc(sketch, "E80.17", {"start": v(37.9, 70.2) * mm, "mid": v(94.05, 50.88) * mm, "end": v(150.2, 70.2) * mm});
            skArc(sketch, "E80.18", {"start": v(150.2, 70.2) * mm, "mid": v(153.04, 73.7) * mm, "end": v(154.05, 78.09) * mm});
            skLineSegment(sketch, "E80.19", {"start": v(154.05, 158.68) * mm, "end": v(154.05, 78.09) * mm});
            skArc(sketch, "E80.20", {"start": v(154.05, 158.68) * mm, "mid": v(153.04, 163.06) * mm, "end": v(150.2, 166.56) * mm});
            skCircle(sketch, "E81", {"center": v(94.05, 238.38) * mm, "radius": 6 * mm});
            skArc(sketch, "E82", {"start": v(109.05, 238.38) * mm, "mid": v(94.05, 253.38) * mm, "end": v(79.05, 238.38) * mm});
            skLineSegment(sketch, "E83", {"start": v(79.05, 238.38) * mm, "end": v(79.05, 226.38) * mm});
            skLineSegment(sketch, "E84", {"start": v(109.05, 238.38) * mm, "end": v(109.05, 226.38) * mm});
            skLineSegment(sketch, "E85", {"start": v(109.05, 226.38) * mm, "end": v(127.05, 208.38) * mm});
            skLineSegment(sketch, "E86", {"start": v(79.05, 226.38) * mm, "end": v(61.05, 208.38) * mm});
            skLineSegment(sketch, "E87", {"start": v(94.05, 238.38) * mm, "end": v(94.05, 208.38) * mm, "construction": true});
            skLineSegment(sketch, "E88", {"start": v(14.05, 118.38) * mm, "end": v(174.05, 118.38) * mm, "construction": true});
            skLineSegment(sketch, "E89.MirrorCS", {"start": v(79.05, 10.38) * mm, "end": v(61.05, 28.38) * mm});
            skLineSegment(sketch, "E90.MirrorCS", {"start": v(109.05, 10.38) * mm, "end": v(127.05, 28.38) * mm});
            skLineSegment(sketch, "E91.MirrorCS", {"start": v(109.05, -1.62) * mm, "end": v(109.05, 10.38) * mm});
            skArc(sketch, "E92.MirrorCS", {"start": v(109.05, -1.62) * mm, "mid": v(94.05, -16.62) * mm, "end": v(79.05, -1.62) * mm});
            skLineSegment(sketch, "E93.MirrorCS", {"start": v(79.05, -1.62) * mm, "end": v(79.05, 10.38) * mm});
            skLineSegment(sketch, "E94.MirrorCS", {"start": v(94.05, -1.62) * mm, "end": v(94.05, 28.38) * mm, "construction": true});
            skCircle(sketch, "E95.MirrorC", {"center": v(94.05, -1.62) * mm, "radius": 6 * mm});
            skSolve(sketch);
        }
        {
            var Q0;
            Q0=makeQuery(id+"F16.imprint","IMPRINT",FACE,{"disambiguationData":[TD([[makeQuery(id+"F16.imprint","IMPRINT",EDGE,{"derivedFrom":sQuery(id+"F16.wireOp",EDGE,"E81")}),-1.0]])]});
            var Q1;
            {var subQ2=sQuery(id+"F16.wireOp",EDGE,"E89.MirrorCS");Q1=makeQuery(id+"F16.imprint","IMPRINT",FACE,{"disambiguationData":[TD([[makeQuery(id+"F16.imprint","IMPRINT",EDGE,{"derivedFrom":subQ2}),-1.0]])]});}
            var Q2;
            Q2=makeQuery(id+"F1.opExtrude","CAP_FACE",FACE,{"disambiguationData":[OSD([sQuery(id+"F0.wireOp",EDGE,"E1.bottom"),sQuery(id+"F0.wireOp",EDGE,"E1.top"),sQuery(id+"F0.wireOp",EDGE,"E1.left"),sQuery(id+"F0.wireOp",EDGE,"E1.right"),sQuery(id+"F0.wireOp",EDGE,"E4"),sQuery(id+"F0.wireOp",EDGE,"E5"),sQuery(id+"F0.wireOp",EDGE,"E6"),sQuery(id+"F0.wireOp",EDGE,"E7"),sQuery(id+"F0.wireOp",EDGE,"E21.filletArc"),sQuery(id+"F0.wireOp",EDGE,"E22.filletArc"),sQuery(id+"F0.wireOp",EDGE,"E23.filletArc"),sQuery(id+"F0.wireOp",EDGE,"E24.filletArc")])],"isStart":false});
            extrude(context, id + "F17", {"entities" : qUnion([Q0, Q1]), "operationType" : NewBodyOperationType.ADD, "endBound" : BoundingType.UP_TO_SURFACE, "oppositeDirection" : true, "endBoundEntityFace" : qUnion([Q2]), "depth" : 25 * mm});
        }
    });
